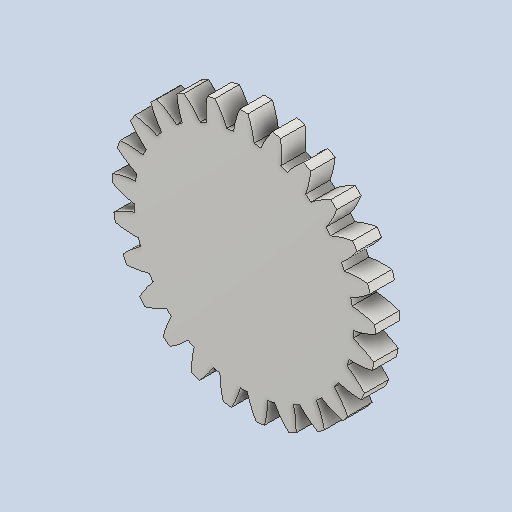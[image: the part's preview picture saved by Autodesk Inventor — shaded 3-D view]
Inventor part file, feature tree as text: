
AUTODESK INVENTOR PART (.ipt)
format: ipt  version: 2024 (Build 280153000, 153)  size: 244,736 bytes
history: native  units: mm (DEFAULTED — no unit token found)
features: plane x3, other x3, extrude x1, sketch x1
ambient origin geometry x8: Origin, YZ Plane, XZ Plane, XY Plane, X Axis, Y Axis, Z Axis, Center Point
bodies: Solid1 (feature_tree)
feature tree (8):
  extrude  "Extrusion1"  Depth=5.0mm TaperAngle=0.0deg
  plane  "Work Plane2"
  plane  "Work Plane8"
  plane  "Work Plane9"
  other  "Spur Gear"
  sketch  "Sketch1"  dims[d0=54.0mm d1=5.0mm d2=0.0mm d3=50.0mm d4=10.0mm d5=0.0mm d16=35.0mm d17=0.0mm d34=1.256637mm d39=0.0mm d41=0.0mm d43=35.0mm d46=35.0mm d47=0.0mm d48=0.0mm]
  other  "Srf1"
  other  "Pitch Diameter"
